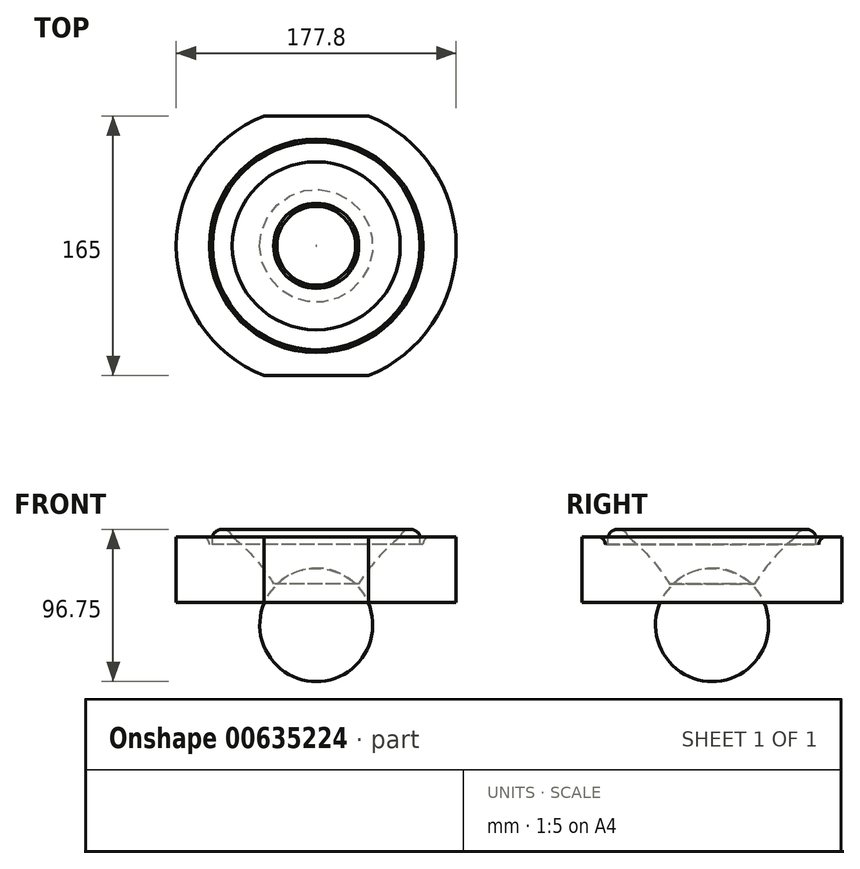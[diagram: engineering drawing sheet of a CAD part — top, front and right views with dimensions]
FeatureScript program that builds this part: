
annotation { "Feature Type Name" : "Feature", "Feature Type Description" : "" }
export const myFeature = defineFeature(function(context is Context, id is Id, definition is map)
    precondition{}
    {
        {
            var Q0;
            Q0=qCreatedBy(makeId("Front.planeOp"),FACE);
            var sketch = newSketch(context, id + "F0", { "sketchPlane" : qUnion([Q0])});
            skArc(sketch, "E0", {"start": v(-53.33, 0.01) * mm, "mid": v(-59.67, 4.75) * mm, "end": v(-66, 0) * mm});
            skArc(sketch, "E1", {"start": v(0, -20) * mm, "mid": v(-13.47, -22.57) * mm, "end": v(-25, -30) * mm});
            skLineSegment(sketch, "E2", {"start": v(-25, -30) * mm, "end": v(-27, -30) * mm});
            skArc(sketch, "E3", {"start": v(-67.83, -4.93) * mm, "mid": v(-69.31, -1.44) * mm, "end": v(-72.82, 0) * mm});
            skLineSegment(sketch, "E4", {"start": v(-67.83, -4.93) * mm, "end": v(-66, -4.93) * mm});
            skLineSegment(sketch, "E5", {"start": v(-88.9, 0) * mm, "end": v(-88.9, -41.8) * mm});
            skLineSegment(sketch, "E6", {"start": v(-88.9, -41.8) * mm, "end": v(0, -41.8) * mm});
            skLineSegment(sketch, "E7", {"start": v(0, -41.8) * mm, "end": v(0, -20) * mm});
            skLineSegment(sketch, "E8", {"start": v(0, 57.74) * mm, "end": v(0, -80.71) * mm, "construction": true});
            skLineSegment(sketch, "E9", {"start": v(-66, 0) * mm, "end": v(-66, -4.93) * mm});
            skLineSegment(sketch, "E10", {"start": v(-72.82, 0) * mm, "end": v(-88.9, 0) * mm});
            skArc(sketch, "E11", {"start": v(-27, -30) * mm, "mid": v(-38.89, -13.87) * mm, "end": v(-53.33, 0.01) * mm});
            skSolve(sketch);
        }
        {
            var Q0;
            Q0 = qSketchRegion(id + "F0", true);
            var Q1;
            Q1=sQuery(id+"F0.wireOp",EDGE,"E8");
            revolve(context, id + "F1", {"entities" : qUnion([Q0]), "axis" : qUnion([Q1]), "revolveType" : RevolveType.FULL});
        }
        {
            var Q0;
            Q0=makeQuery(id+"F1.opRevolve","SWEPT_FACE",FACE,{"disambiguationData":[OSD([sQuery(id+"F0.wireOp",EDGE,"E10")])]});
            var sketch = newSketch(context, id + "F2", { "sketchPlane" : qUnion([Q0])});
            skLineSegment(sketch, "E12", {"start": v(-33.12, 82.5) * mm, "end": v(33.12, 82.5) * mm});
            skLineSegment(sketch, "E13", {"start": v(-33.12, -82.5) * mm, "end": v(33.12, -82.5) * mm});
            skLineSegment(sketch, "E14", {"start": v(-33.12, -82.5) * mm, "end": v(-49.08, -82.5) * mm});
            skLineSegment(sketch, "E15", {"start": v(-49.08, -82.5) * mm, "end": v(6.97, -111.72) * mm});
            skLineSegment(sketch, "E16", {"start": v(6.97, -111.72) * mm, "end": v(56.65, -82.5) * mm});
            skLineSegment(sketch, "E17", {"start": v(56.65, -82.5) * mm, "end": v(33.12, -82.5) * mm});
            skLineSegment(sketch, "E18", {"start": v(33.12, 82.5) * mm, "end": v(63.94, 82.5) * mm});
            skLineSegment(sketch, "E19", {"start": v(63.94, 82.5) * mm, "end": v(-2.14, 104.54) * mm});
            skLineSegment(sketch, "E20", {"start": v(-2.14, 104.54) * mm, "end": v(-59.57, 82.5) * mm});
            skLineSegment(sketch, "E21", {"start": v(-59.57, 82.5) * mm, "end": v(-33.12, 82.5) * mm});
            skSolve(sketch);
        }
        {
            var Q0;
            Q0 = qSketchRegion(id + "F2", true);
            extrude(context, id + "F3", {"entities" : qUnion([Q0]), "operationType" : NewBodyOperationType.REMOVE, "endBound" : BoundingType.THROUGH_ALL, "oppositeDirection" : true, "depth" : 25 * mm, "offsetDistance" : 25 * mm});
        }
    });
